# Revit family: Sanitary_Showers_hansgrohe_24241SGP-Pulsify-Showerpipe-260-2jet-2-t_
name_source: partatom
category: Plumbing Fixtures
revit_build: Autodesk Revit 2018 (Build: 20170223_1515(x64)
units: mm (PartAtom-declared; Revit-internal decimal feet)

## family parameters
Always vertical = No
Cut with Voids When Loaded = No
OmniClass Number = 23.45.00.00
OmniClass Title = Sanitary, Laundry, and Cleaning Equipment
Part Type = Normal
Room Calculation Point = No
Round Connector Dimension = Use Diameter
Shared = No
Work Plane-Based = Yes

## types (3) — shared parameters
Always visible = Yes
BIMobject category = Showers
Default Elevation = 1219.2 mm  [stored 4 ft]
Design country = Germany
Edition number = 1
IFC Classification = Sanitary Terminal
Installation instructions = https://www.hansgrohe.com
Manufacturer country = Germany
Manufacturer name = hansgrohe
Material 2 = Hansgrohe - Pulsify - Graphite
Material main = Chrome
Product Guid = 512a3830-a1b1-436c-85d2-6e1d150f2f64
Product SKU = 24241SGP
Product data url = https://www.bimobject.com
Product family = Pulsify
Product group = Showerpipes with thermostat
Product name = 24241SGP Pulsify Showerpipe 260 2jet 2 ticks with ShowerTablet Select 400
Product url = https://www.hansgrohe.com
QR code = https://www.bimobject.com
Technical description = https://www.hansgrohe.com

## per-type parameters (varying)
| type | Material 1 |
| 709 Matt White | Hansgrohe - Pulsify - 709 Matt White |
| 679 Matte Black | Hansgrohe - Pulsify - 679 Matte Black |
| 009 Chrome | Hansgrohe - Pulsify - 009 Chrome |

note: [stored X ft] marks values corroborated as IEEE doubles in the binary element streams (Revit-internal decimal feet)

## geometry (parser evidence)
native form markers: Sweep x1
no freeform markers — native parametric forms only
